# Revit family: TermCon_DN20_MM_RFA_2019
name_source: partatom
category: Pipe Accessories
units: mm (PartAtom-declared; Revit-internal decimal feet)

## family parameters
Always vertical = Yes
Cut with Voids When Loaded = No
Part Type = Valve - Breaks Into
Round Connector Dimension = Use Diameter
Shared = No
Work Plane-Based = No

## types (1)
- TemCon DN20 M/M
    CenSd_R3_6 = 13 mm  [stored 0.0426509 ft]
    D = 20 mm
    DT2 = 10 mm  [stored 0.0328084 ft]
    Description = Automatický termostatický vyvažovací ventil pro rozvody TUV
    H1 = 18 mm  [stored 0.0590551 ft]
    H2 = 4 mm  [stored 0.0131234 ft]
    H3 = 11 mm  [stored 0.0360892 ft]
    H4 = 39 mm
    L1 = 18 mm  [stored 0.0590551 ft]
    L2 = 27 mm  [stored 0.0885827 ft]
    L2D = 38 mm
    L2D_Min = 30 mm  [stored 0.0984252 ft]
    LL = 15 mm  [stored 0.0492126 ft]
    LL1 = 4 mm  [stored 0.0131234 ft]
    LL1__ve = -4 mm
    LL__ve = -15 mm  [stored -0.0492126 ft]
    LT2 = 34 mm
    MC Product Code = 47-2892 DN20 MM (37-65°C, max 100kPa)
    Manufacturer = Hydronic Systems Prague s.r.o.
    QmdConnectorList = 301;D;302;D
    R1 = 15 mm  [stored 0.0492126 ft]
    R2 = 14 mm  [stored 0.0459318 ft]
    R3 = 15 mm  [stored 0.0492126 ft]
    R4 = 16 mm
    R5 = 13 mm  [stored 0.0426509 ft]
    R6 = 13 mm  [stored 0.0426509 ft]
    R7 = 12 mm  [stored 0.0393701 ft]
    Type Comments = závitový s vnějším závitem PN10;  max dp=100kPa; pracovní rozsah 10+-100°C; rozsah nastavení 37-65°C; rouzsah nastavení pro bypass 70-80°C;
    URL = www.hydronic.cz
    W = 42 mm  [stored 0.137795 ft]
    W1 = 24 mm  [stored 0.0787402 ft]
    W2 = 2 mm  [stored 0.00656168 ft]
    W2D = 20 mm  [stored 0.0656168 ft]
    magiPartTypeId = 306
    magiProductFamilyId = 21dbfbd9cdbe4438ac6817ff3d9771
    magiProductId = 6f633da33f234d7083190c3661a0b3

note: [stored X ft] marks values corroborated as IEEE doubles in the binary element streams (Revit-internal decimal feet)
